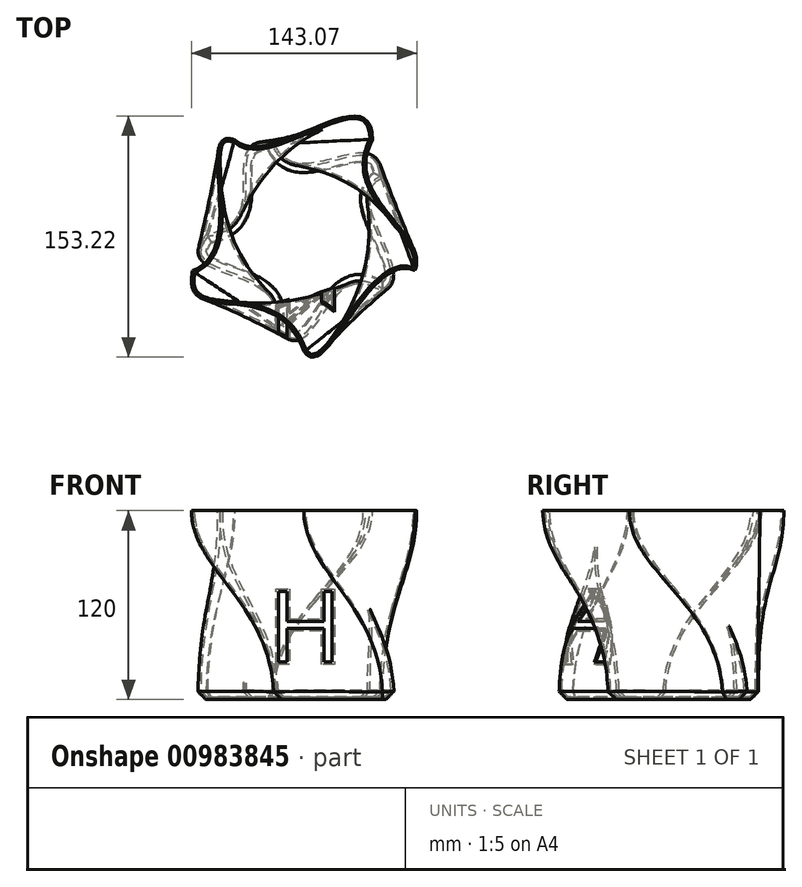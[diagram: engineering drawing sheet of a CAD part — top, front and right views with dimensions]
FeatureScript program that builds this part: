
annotation { "Feature Type Name" : "Feature", "Feature Type Description" : "" }
export const myFeature = defineFeature(function(context is Context, id is Id, definition is map)
    precondition{}
    {
        {
            var Q0;
            Q0=qCreatedBy(makeId("Top.planeOp"),FACE);
            cPlane(context, id + "F0", {"entities" : qUnion([Q0]), "cplaneType" : CPlaneType.OFFSET, "offset" : 120 * mm, "width" : 150 * mm, "height" : 150 * mm});
        }
        {
            var Q0;
            Q0=qCreatedBy(makeId("Top.planeOp"),FACE);
            var sketch = newSketch(context, id + "F1", { "sketchPlane" : qUnion([Q0])});
            skCircle(sketch, "E0.cCircle", {"center": v(0, 0) * mm, "radius": 50 * mm, "construction": true});
            skLineSegment(sketch, "E0.0", {"start": v(50, 36.33) * mm, "end": v(50, -36.33) * mm, "construction": true});
            skLineSegment(sketch, "E0.1", {"start": v(50, -36.33) * mm, "end": v(-19.1, -58.78) * mm, "construction": true});
            skLineSegment(sketch, "E0.2", {"start": v(-19.1, -58.78) * mm, "end": v(-61.8, 0) * mm, "construction": true});
            skLineSegment(sketch, "E0.3", {"start": v(-61.8, 0) * mm, "end": v(-19.1, 58.78) * mm, "construction": true});
            skLineSegment(sketch, "E0.4", {"start": v(-19.1, 58.78) * mm, "end": v(50, 36.33) * mm, "construction": true});
            skPoint(sketch, "E0.0.midPoint", {"position": v(50, 0) * mm});
            skFitSpline(sketch, "E1", {"points": [v(-19.1, 58.78) * mm, v(50, 36.33) * mm], "startDerivative": vector(40.38, -111.76) * mm, "endDerivative": vector(7.12, -121.17) * mm});
            skFitSpline(sketch, "E2", {"points": [v(50, 36.33) * mm, v(50, -36.33) * mm], "startDerivative": vector(-84.13, -40.56) * mm, "endDerivative": vector(-77.6, -33) * mm});
            skFitSpline(sketch, "E3", {"points": [v(50, -36.33) * mm, v(-19.1, -58.78) * mm], "startDerivative": vector(-114.93, 81.14) * mm, "endDerivative": vector(-88.51, 105.65) * mm});
            skFitSpline(sketch, "E4", {"points": [v(-19.1, -58.78) * mm, v(-61.8, 0) * mm], "startDerivative": vector(34.6, 125.4) * mm, "endDerivative": vector(79.87, 97.15) * mm});
            skFitSpline(sketch, "E5", {"points": [v(-61.8, 0) * mm, v(-19.1, 58.78) * mm], "startDerivative": vector(137.69, 20.3) * mm, "endDerivative": vector(123.27, -13.39) * mm});
            skSolve(sketch);
        }
        {
            var Q0;
            Q0=qCreatedBy(id+"F0.planeOp",FACE);
            var sketch = newSketch(context, id + "F2", { "sketchPlane" : qUnion([Q0])});
            skCircle(sketch, "E6.cCircle", {"center": v(0, 0) * mm, "radius": 60 * mm, "construction": true});
            skLineSegment(sketch, "E6.0", {"start": v(-43.6, 60) * mm, "end": v(43.6, 60) * mm, "construction": true});
            skLineSegment(sketch, "E6.1", {"start": v(43.6, 60) * mm, "end": v(70.53, -22.92) * mm, "construction": true});
            skLineSegment(sketch, "E6.2", {"start": v(70.53, -22.92) * mm, "end": v(0, -74.16) * mm, "construction": true});
            skLineSegment(sketch, "E6.3", {"start": v(0, -74.16) * mm, "end": v(-70.53, -22.92) * mm, "construction": true});
            skLineSegment(sketch, "E6.4", {"start": v(-70.53, -22.92) * mm, "end": v(-43.6, 60) * mm, "construction": true});
            skPoint(sketch, "E6.0.midPoint", {"position": v(0, 60) * mm});
            skFitSpline(sketch, "E7", {"points": [v(-43.6, 60) * mm, v(43.6, 60) * mm], "startDerivative": vector(66.98, -61.4) * mm, "endDerivative": vector(-0.25, -129.26) * mm});
            skFitSpline(sketch, "E8", {"points": [v(43.6, 60) * mm, v(70.53, -22.92) * mm], "startDerivative": vector(-59.6, -107.74) * mm, "endDerivative": vector(-30, -68.75) * mm});
            skFitSpline(sketch, "E9", {"points": [v(70.53, -22.92) * mm, v(0, -74.16) * mm], "startDerivative": vector(-87.56, 40.98) * mm, "endDerivative": vector(-42.16, 67.47) * mm});
            skFitSpline(sketch, "E10", {"points": [v(0, -74.16) * mm, v(-70.53, -22.92) * mm], "startDerivative": vector(-52.25, 149.96) * mm, "endDerivative": vector(25.6, 115.53) * mm});
            skFitSpline(sketch, "E11", {"points": [v(-70.53, -22.92) * mm, v(-43.6, 60) * mm], "startDerivative": vector(108.38, 40.5) * mm, "endDerivative": vector(82.25, -32.05) * mm});
            skSolve(sketch);
        }
        {
            var Q0;
            Q0=makeQuery(id+"F1.imprint","IMPRINT",FACE,{"disambiguationData":[TD([[makeQuery(id+"F1.imprint","IMPRINT",EDGE,{"derivedFrom":sQuery(id+"F1.wireOp",EDGE,"E1")}),-1.0]])]});
            var Q1;
            Q1=makeQuery(id+"F2.imprint","IMPRINT",FACE,{"disambiguationData":[TD([[makeQuery(id+"F2.imprint","IMPRINT",EDGE,{"derivedFrom":sQuery(id+"F2.wireOp",EDGE,"E7")}),-1.0]])]});
            var Q2;
            Q2=sQuery(id+"F1.wireOp",VERTEX,"E0.2.end");
            var Q3;
            Q3=sQuery(id+"F2.wireOp",VERTEX,"E6.0.start");
            loft(context, id + "F3", {"startCondition" : LoftEndDerivativeType.NORMAL_TO_PROFILE, "startMagnitude" : 1.5, "endCondition" : LoftEndDerivativeType.NORMAL_TO_PROFILE, "endMagnitude" : 1, "sheetProfilesArray" : [{ "sheetProfileEntities" : qUnion([Q0]) }, { "sheetProfileEntities" : qUnion([Q1]) }], "matchConnections" : true, "connections" : [{ "connectionEntities" : qUnion([Q2, Q3]), "connectionEdgeQueries" : qUnion([]), "connectionEdgeParameters" : [] }]});
        }
        {
            var Q0;
            Q0=makeQuery(id+"F3.opLoft","CAP_FACE",FACE,{"disambiguationData":[OSD([makeQuery(id+"F1.imprint","IMPRINT",FACE,{"disambiguationData":[TD([[makeQuery(id+"F1.imprint","IMPRINT",EDGE,{"derivedFrom":sQuery(id+"F1.wireOp",EDGE,"E1")}),-1.0]])]})])],"isStart":true});
            chamfer(context, id + "F4", {"entities" : qUnion([Q0]), "width" : 5 * mm, "tangentPropagation" : true});
        }
        {
            var Q0;
            Q0=qCreatedBy(makeId("Front.planeOp"),FACE);
            cPlane(context, id + "F5", {"entities" : qUnion([Q0]), "cplaneType" : CPlaneType.OFFSET, "offset" : 100 * mm, "width" : 150 * mm, "height" : 150 * mm});
        }
        {
            var Q0;
            Q0=qCreatedBy(id+"F5.planeOp",FACE);
            var sketch = newSketch(context, id + "F6", { "sketchPlane" : qUnion([Q0])});
            skText(sketch, "E12", { "text": "H", "fontName": "OpenSans-Regular.ttf"});
            const initialGuessF6  = {"E12": [-0.0221, 0.024, 1, 0, 0.04513]};
            skSetInitialGuess(sketch, initialGuessF6);
            skSolve(sketch);
        }
        {
            var Q0;
            Q0 = qSketchRegion(id + "F6", true);
            extrude(context, id + "F7", {"entities" : qUnion([Q0]), "operationType" : NewBodyOperationType.REMOVE, "endBound" : BoundingType.UP_TO_NEXT, "oppositeDirection" : true, "depth" : 25 * mm, "hasOffset" : true, "offsetDistance" : 1 * mm, "offsetOppositeDirection" : true});
        }
        {
            var Q0;
            Q0=qCreatedBy(makeId("Front.planeOp"),FACE);
            var sketch = newSketch(context, id + "F8", { "sketchPlane" : qUnion([Q0])});
            skLineSegment(sketch, "E13", {"start": v(0, 0) * mm, "end": v(0, 131.05) * mm, "construction": true});
            skSolve(sketch);
        }
        {
            var Q0;
            Q0=makeQuery(id+"F3.opLoft","CAP_FACE",FACE,{"disambiguationData":[OSD([makeQuery(id+"F2.imprint","IMPRINT",FACE,{"disambiguationData":[TD([[makeQuery(id+"F2.imprint","IMPRINT",EDGE,{"derivedFrom":sQuery(id+"F2.wireOp",EDGE,"E7")}),-1.0]])]})])],"isStart":true});
            shell(context, id + "F9", {"entities" : qUnion([Q0]), "thickness" : 1.6 * mm});
        }
    });
